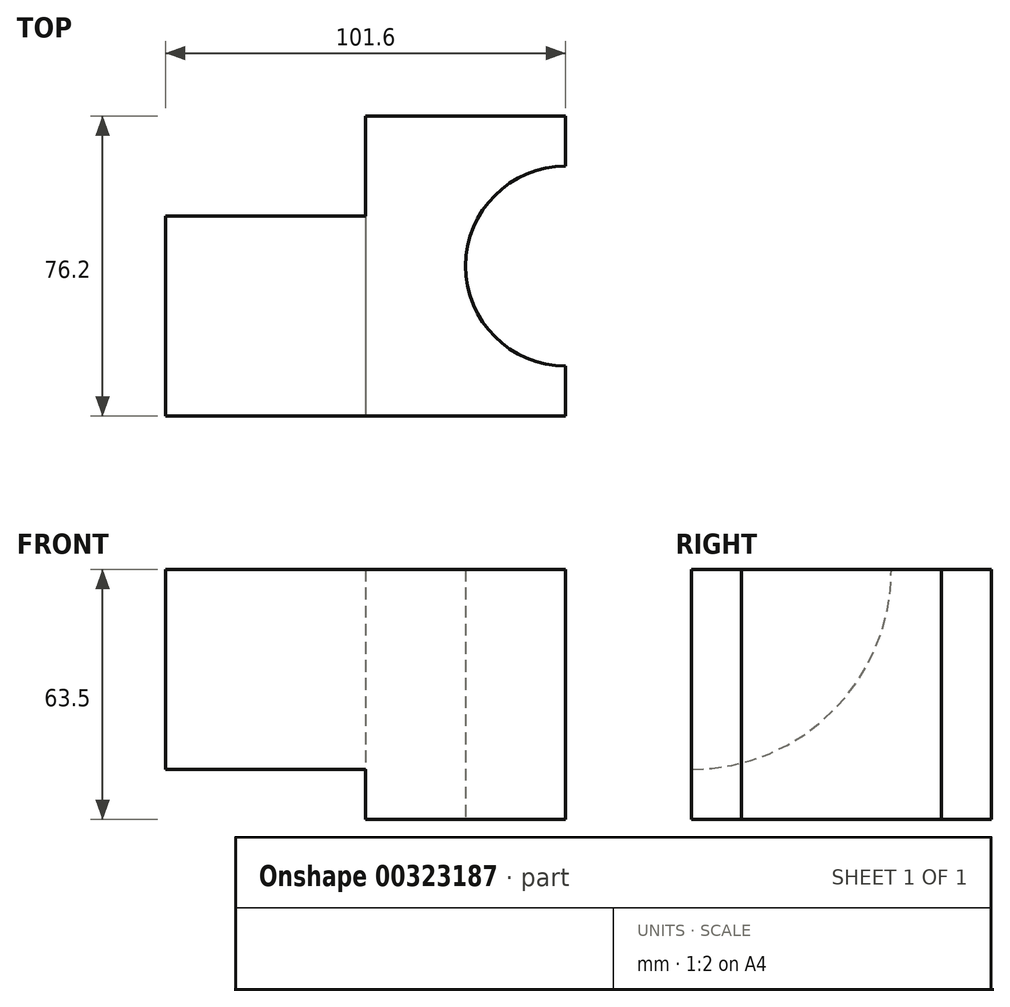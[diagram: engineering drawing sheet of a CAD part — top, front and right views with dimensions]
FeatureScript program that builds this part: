
annotation { "Feature Type Name" : "Feature", "Feature Type Description" : "" }
export const myFeature = defineFeature(function(context is Context, id is Id, definition is map)
    precondition{}
    {
        {
            var Q0;
            Q0=qCreatedBy(makeId("Top.planeOp"),FACE);
            var sketch = newSketch(context, id + "F0", { "sketchPlane" : qUnion([Q0])});
            skLineSegment(sketch, "E0.bottom", {"start": v(50.8, 38.1) * mm, "end": v(-50.8, 38.1) * mm});
            skLineSegment(sketch, "E0.top", {"start": v(50.8, -38.1) * mm, "end": v(-50.8, -38.1) * mm});
            skLineSegment(sketch, "E0.left", {"start": v(50.8, 38.1) * mm, "end": v(50.8, -38.1) * mm});
            skLineSegment(sketch, "E0.right", {"start": v(-50.8, 38.1) * mm, "end": v(-50.8, -38.1) * mm});
            skPoint(sketch, "E0.middle", {"position": v(0, 0) * mm});
            skArc(sketch, "E1", {"start": v(50.8, 25.4) * mm, "mid": v(25.4, 0) * mm, "end": v(50.8, -25.4) * mm});
            skSolve(sketch);
        }
        {
            var Q0;
            {var subQ3=sQuery(id+"F0.wireOp",EDGE,"E0.bottom");Q0=makeQuery(id+"F0.imprint","IMPRINT",FACE,{"disambiguationData":[TD([[makeQuery(id+"F0.imprint","IMPRINT",EDGE,{"derivedFrom":subQ3}),1.0]])]});}
            extrude(context, id + "F1", {"entities" : qUnion([Q0]), "depth" : 63.5 * mm});
        }
        {
            var Q0;
            Q0=makeQuery(id+"F1.opExtrude","SWEPT_FACE",FACE,{"disambiguationData":[OSD([sQuery(id+"F0.wireOp",EDGE,"E0.right")])]});
            var sketch = newSketch(context, id + "F2", { "sketchPlane" : qUnion([Q0])});
            skArc(sketch, "E2", {"start": v(38.1, 12.7) * mm, "mid": v(2.18, 27.58) * mm, "end": v(-12.7, 63.5) * mm});
            skLineSegment(sketch, "E3", {"start": v(-12.7, 63.5) * mm, "end": v(38.1, 63.5) * mm});
            skLineSegment(sketch, "E4", {"start": v(38.1, 63.5) * mm, "end": v(38.1, 12.7) * mm});
            skSolve(sketch);
        }
        {
            var Q0;
            Q0=makeQuery(id+"F2.imprint","IMPRINT",FACE,{"disambiguationData":[TD([[makeQuery(id+"F2.imprint","IMPRINT",EDGE,{"derivedFrom":sQuery(id+"F2.wireOp",EDGE,"E2")}),-1.0]])]});
            extrude(context, id + "F3", {"entities" : qUnion([Q0]), "operationType" : NewBodyOperationType.REMOVE, "oppositeDirection" : true, "depth" : 50.8 * mm});
        }
    });
